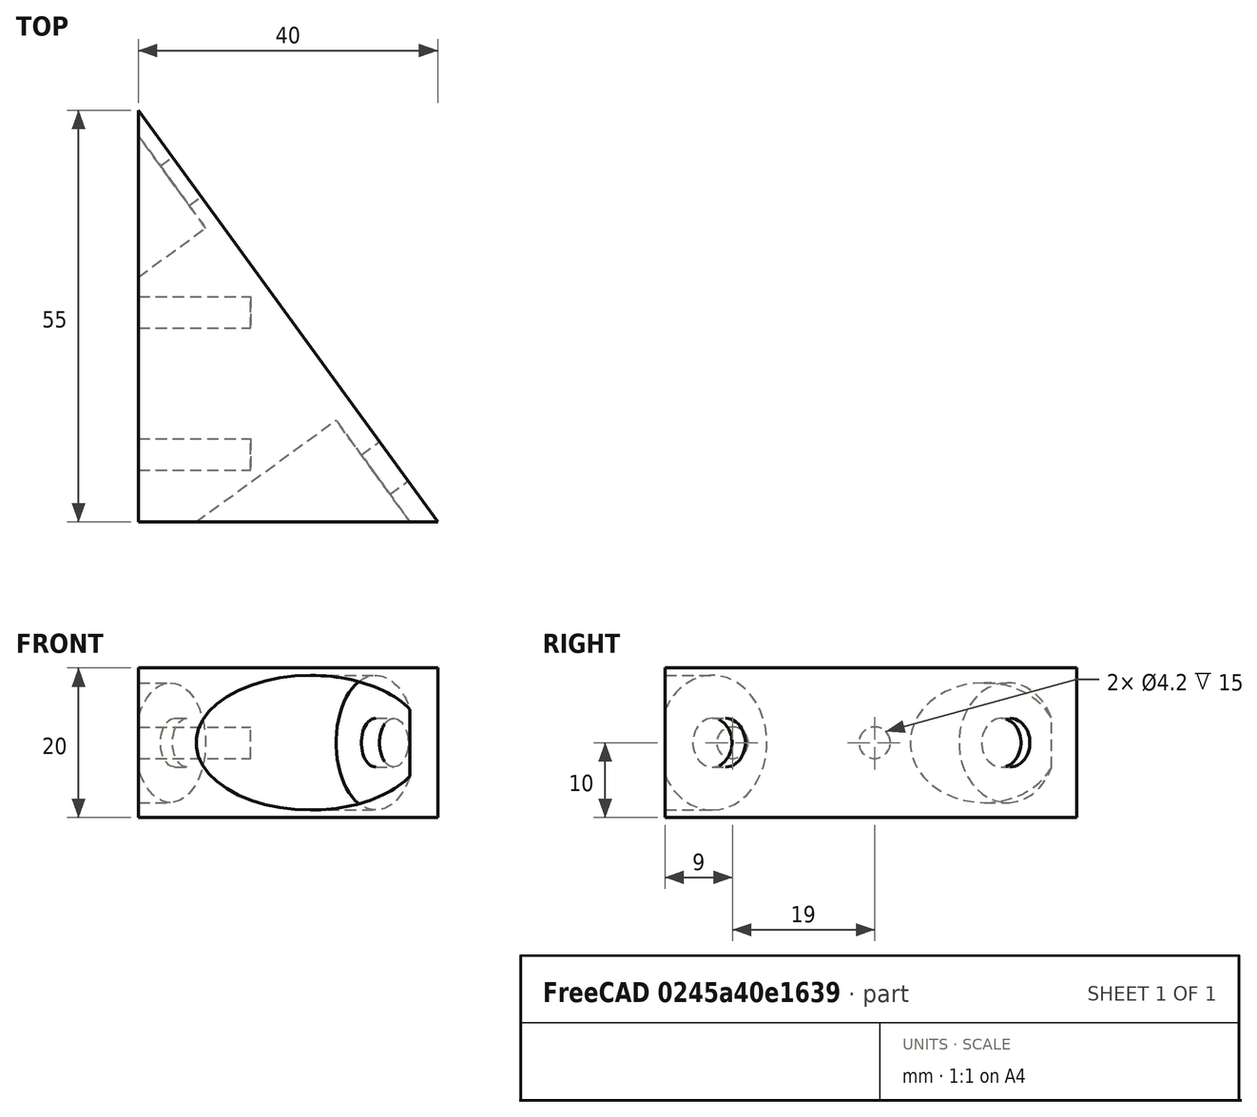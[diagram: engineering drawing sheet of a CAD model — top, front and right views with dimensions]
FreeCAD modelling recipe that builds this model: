
FCSTD DOCUMENT  (FreeCAD 0.19R22846 (Git))
Label: rainsensor_keil
License: All rights reserved
LicenseURL: http://en.wikipedia.org/wiki/All_rights_reserved
objects: Part::Cylinder×6, Part::Cut×6, Part::Wedge×1
note: 13 computed .brp shape members not serialized (recipe doc carries the construction recipe); baked Part::Feature solids carry a one-line shape summary decoded from their .brp

FEATURE [Part::Wedge] Wedge  label="Keil"
  AttacherType = Attacher::AttachEngine3D
  X2max = 0
  X2min = 0
  Xmax = 40
  Xmin = 0
  Ymax = 55
  Ymin = 0
  Z2max = 20
  Z2min = 0
  Zmax = 20
  Zmin = 0
FEATURE [Part::Cylinder] Cylinder  label="Zylinder"
  Angle = 360
  AttacherType = Attacher::AttachEngine3D
  Height = 15
  Placement = pos=(0,9,10) rot=(0,1,0;1.5708rad)
  Radius = 2.1
FEATURE [Part::Cylinder] Cylinder001  label="Zylinder001"
  Angle = 360
  AttacherType = Attacher::AttachEngine3D
  Height = 15
  Placement = pos=(0,28,10) rot=(0,1,0;1.5708rad)
  Radius = 2.1
FEATURE [Part::Cylinder] Cylinder002  label="Zylinder002"
  Angle = 360
  AttacherType = Attacher::AttachEngine3D
  Height = 30
  Placement = pos=(14.7065,-6.02579,10) rot=(-0.29544,0.908532,0.29544;1.66657rad)
  Radius = 3.25
FEATURE [Part::Cylinder] Cylinder003  label="Zylinder003"
  Angle = 360
  AttacherType = Attacher::AttachEngine3D
  Height = 30
  Placement = pos=(-13.7464,31.3966,10) rot=(-0.29544,0.908532,0.29544;1.66657rad)
  Radius = 3.25
FEATURE [Part::Cylinder] Cylinder004  label="Zylinder004"
  Angle = 360
  AttacherType = Attacher::AttachEngine3D
  Height = 29
  Placement = pos=(8.23657,-10.7312,10) rot=(-0.29544,0.908532,0.29544;1.66657rad)
  Radius = 9
FEATURE [Part::Cylinder] Cylinder005  label="Zylinder005"
  Angle = 360
  AttacherType = Attacher::AttachEngine3D
  Height = 22
  Placement = pos=(-13.5258,32.7935,10) rot=(-0.29544,0.908532,0.29544;1.66657rad)
  Radius = 8
FEATURE [Part::Cut] Cut
  Base = -> Wedge
  Tool = -> Cylinder
FEATURE [Part::Cut] Cut001
  Base = -> Cut
  Tool = -> Cylinder001
FEATURE [Part::Cut] Cut002
  Base = -> Cut001
  Tool = -> Cylinder002
FEATURE [Part::Cut] Cut003
  Base = -> Cut002
  Tool = -> Cylinder003
FEATURE [Part::Cut] Cut004
  Base = -> Cut003
  Tool = -> Cylinder004
FEATURE [Part::Cut] Cut005
  Base = -> Cut004
  Tool = -> Cylinder005
